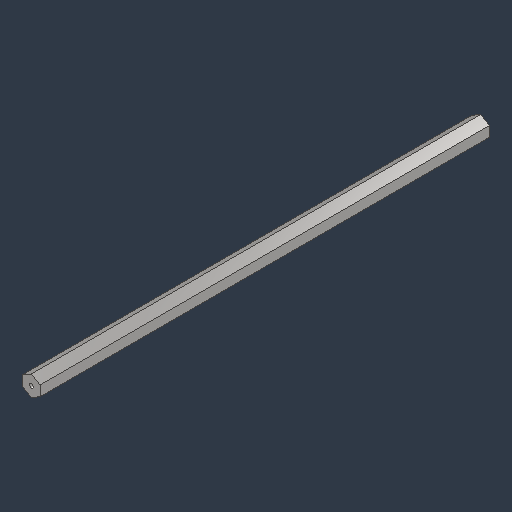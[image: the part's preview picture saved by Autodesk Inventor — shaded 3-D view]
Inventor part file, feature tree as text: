
AUTODESK INVENTOR PART (.ipt)
format: ipt  version: 2024.3 (Build 283343000, 343)  size: 119,296 bytes
history: native  units: in
note: dims shown in document units (in); Inventor stores cm internally (conversion verified against a paired STEP export)
features: extrude x1, sketch x1
ambient origin geometry x8: Origin, YZ Plane, XZ Plane, XY Plane, X Axis, Y Axis, Z Axis, Center Point
bodies: Body1 (feature_tree)
feature tree (2):
  extrude  "Extrusion1"  Depth=12.75in TaperAngle=0.0deg
  sketch  "Sketch1"  dims[d0=0.5in d1=12.75in d2=0.0in d3=0.112in d4=0.0in]
